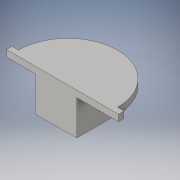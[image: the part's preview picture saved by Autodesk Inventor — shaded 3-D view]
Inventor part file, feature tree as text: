
AUTODESK INVENTOR PART (.ipt)
format: ipt  version: 2016 (Build 200138000, 138)  size: 504,320 bytes
history: native  units: in
note: dims shown in document units (in); Inventor stores cm internally (conversion verified against a paired STEP export)
features: reference x54, extrude x27, sketch x26, plane x6, projected_geometry x2
ambient origin geometry x8: Origin, YZ Plane, XZ Plane, XY Plane, X Axis, Y Axis, Z Axis, Center Point
bodies: Solid1 (feature_tree)
feature tree (115):
  extrude  "Extrusion1"  Depth=3.0in
  extrude  "Extrusion2"  Depth=0.1969in
  extrude  "Extrusion3"  Depth=1.0in
  extrude  "Extrusion4"  Depth=1.0in TaperAngle=0.0deg
  extrude  "Extrusion5"  Depth=0.0197in
  plane  "Work Plane1"
  extrude  "Extrusion6"  Depth=0.0197in
  extrude  "Extrusion7"  Depth=0.0197in
  extrude  "Extrusion8"  Depth=0.0787in
  extrude  "Extrusion9"  Depth=0.303in TaperAngle=0.0deg
  extrude  "Extrusion14"  Depth=0.1575in
  extrude  "Extrusion15"  Depth=0.0098in
  plane  "Work Plane2"
  extrude  "Extrusion16"  Depth=0.1181in TaperAngle=0.0deg
  extrude  "Extrusion17"  Depth=0.1575in
  extrude  "Extrusion18"  Depth=0.1181in TaperAngle=0.0deg
  extrude  "Extrusion19"  Depth=0.0197in
  plane  "Work Plane3"
  extrude  "Extrusion20"  Depth=0.0197in
  extrude  "Extrusion21"  Depth=0.0787in
  plane  "Work Plane4"
  extrude  "Extrusion22"  Depth=1.5748in TaperAngle=0.0deg
  plane  "Work Plane5"
  extrude  "Extrusion23"  Depth=0.9201in TaperAngle=0.0deg
  extrude  "Extrusion24"  Depth=0.1969in
  plane  "Work Plane6"
  extrude  "Extrusion25"  Depth=0.1969in TaperAngle=0.0deg
  extrude  "Extrusion26"  Depth=0.1181in TaperAngle=0.0deg
  extrude  "Extrusion27"  Depth=0.1181in
  extrude  "Extrusion28"  Depth=0.1969in TaperAngle=0.0deg
  extrude  "Extrusion29"  Depth=0.0394in
  extrude  "Extrusion30"  Depth=0.1969in
  extrude  "Extrusion31"  Depth=0.1969in
  sketch  "Sketch1"  dims[d0=4.5in d1=3.0in]
  sketch  "Sketch2"  dims[d2=0.1969in d3=0.0in d5=0.0787in]
  reference  "Reference1"
  reference  "Reference2"
  sketch  "Sketch3"  dims[d6=1.0in d7=0.0in d8=1.0827in]
  sketch  "Sketch4"  dims[d9=0.3937in d10=1.0in d11=0.0in]
  reference  "Reference3"
  reference  "Reference4"
  reference  "Reference5"
  reference  "Reference6"
  reference  "Reference7"
  reference  "Reference8"
  reference  "Reference9"
  reference  "Reference10"
  reference  "Reference11"
  reference  "Reference12"
  reference  "Reference13"
  sketch  "Sketch5"  dims[d12=0.0787in d13=0.0197in]
  reference  "Reference14"
  reference  "Reference15"
  reference  "Reference16"
  reference  "Reference17"
  reference  "Reference18"
  sketch  "Sketch6"  dims[d14=0.0197in d15=0.0197in]
  reference  "Reference19"
  sketch  "Sketch7"  dims[d16=0.0197in d17=0.0197in]
  reference  "Reference20"
  reference  "Reference21"
  reference  "Reference22"
  reference  "Reference23"
  reference  "Reference24"
  sketch  "Sketch8"  dims[d18=0.0787in d19=0.0787in]
  reference  "Reference25"
  sketch  "Sketch9"  dims[d20=0.0787in d21=0.303in d22=0.0in]
  projected_geometry  "Projected Loop1"
  projected_geometry  "Projected Loop2"
  sketch  "Sketch14"  dims[d23=0.0098in d24=0.1575in]
  sketch  "Sketch15"  dims[d25=0.0787in d26=0.0098in]
  sketch  "Sketch16"  dims[d27=0.1575in d28=0.1181in d29=0.0in]
  reference  "Reference30"
  sketch  "Sketch17"  dims[d30=1.25in d31=0.1575in]
  reference  "Reference31"
  reference  "Reference32"
  reference  "Reference33"
  reference  "Reference35"
  reference  "Reference36"
  reference  "Reference37"
  reference  "Reference38"
  reference  "Reference39"
  reference  "Reference40"
  reference  "Reference41"
  reference  "Reference42"
  reference  "Reference43"
  reference  "Reference44"
  reference  "Reference45"
  reference  "Reference46"
  reference  "Reference47"
  reference  "Reference48"
  reference  "Reference49"
  sketch  "Sketch19"  dims[d32=0.1575in d33=0.1181in d34=0.0in]
  sketch  "Sketch20"  dims[d35=0.0197in d36=0.0197in]
  reference  "Reference50"
  sketch  "Sketch21"  dims[d37=0.0197in d38=0.0197in]
  sketch  "Sketch22"  dims[d39=0.0787in d40=0.0787in]
  reference  "Reference51"
  reference  "Reference52"
  sketch  "Sketch23"  dims[d41=0.0787in d42=1.5748in d43=0.0in]
  reference  "Reference53"
  reference  "Reference54"
  sketch  "Sketch24"  dims[d44=0.1801in d45=0.0in d46=0.9201in d47=0.0in]
  sketch  "Sketch25"  dims[d58=0.1969in d59=0.1969in]
  reference  "Reference55"
  reference  "Reference56"
  sketch  "Sketch26"  dims[d60=0.1969in d61=0.1969in d62=0.0in]
  reference  "Reference57"
  reference  "Reference58"
  sketch  "Sketch28"  dims[d63=1.0in d64=0.0in d65=0.1181in d66=0.0in]
  sketch  "Sketch29"  dims[d67=0.1969in d68=0.0in d69=0.1181in]
  sketch  "Sketch30"  dims[d70=0.1181in d71=0.1969in d72=0.0in]
  reference  "Reference59"
  sketch  "Sketch31"  dims[d73=0.0787in d74=0.0in d75=0.0394in]
  sketch  "Sketch32"  dims[d76=0.35in d77=0.1628in d78=0.2in d79=0.0787in d80=0.0in d81=0.1969in d82=0.0in d83=0.0098in d84=0.0787in d85=0.0098in d86=0.0787in d87=0.315in d88=0.0in d89=1.5in d90=1.5in d91=0.1181in d92=0.0in d93=0.7in d94=1.26in d95=0.0in d96=0.1181in d97=0.0in d98=0.1181in d99=0.0in d104=1.0in d105=0.1181in d106=0.5in d107=1.0in d108=0.5in d109=10.0in d110=0.0in d111=0.0197in d112=0.0197in d113=0.325in d114=0.197in d115=0.0in d116=0.1969in d117=0.1969in d118=0.1181in d119=0.1969in d120=0.0in d121=0.1575in d122=0.0in d123=100.0in d124=0.0in]
